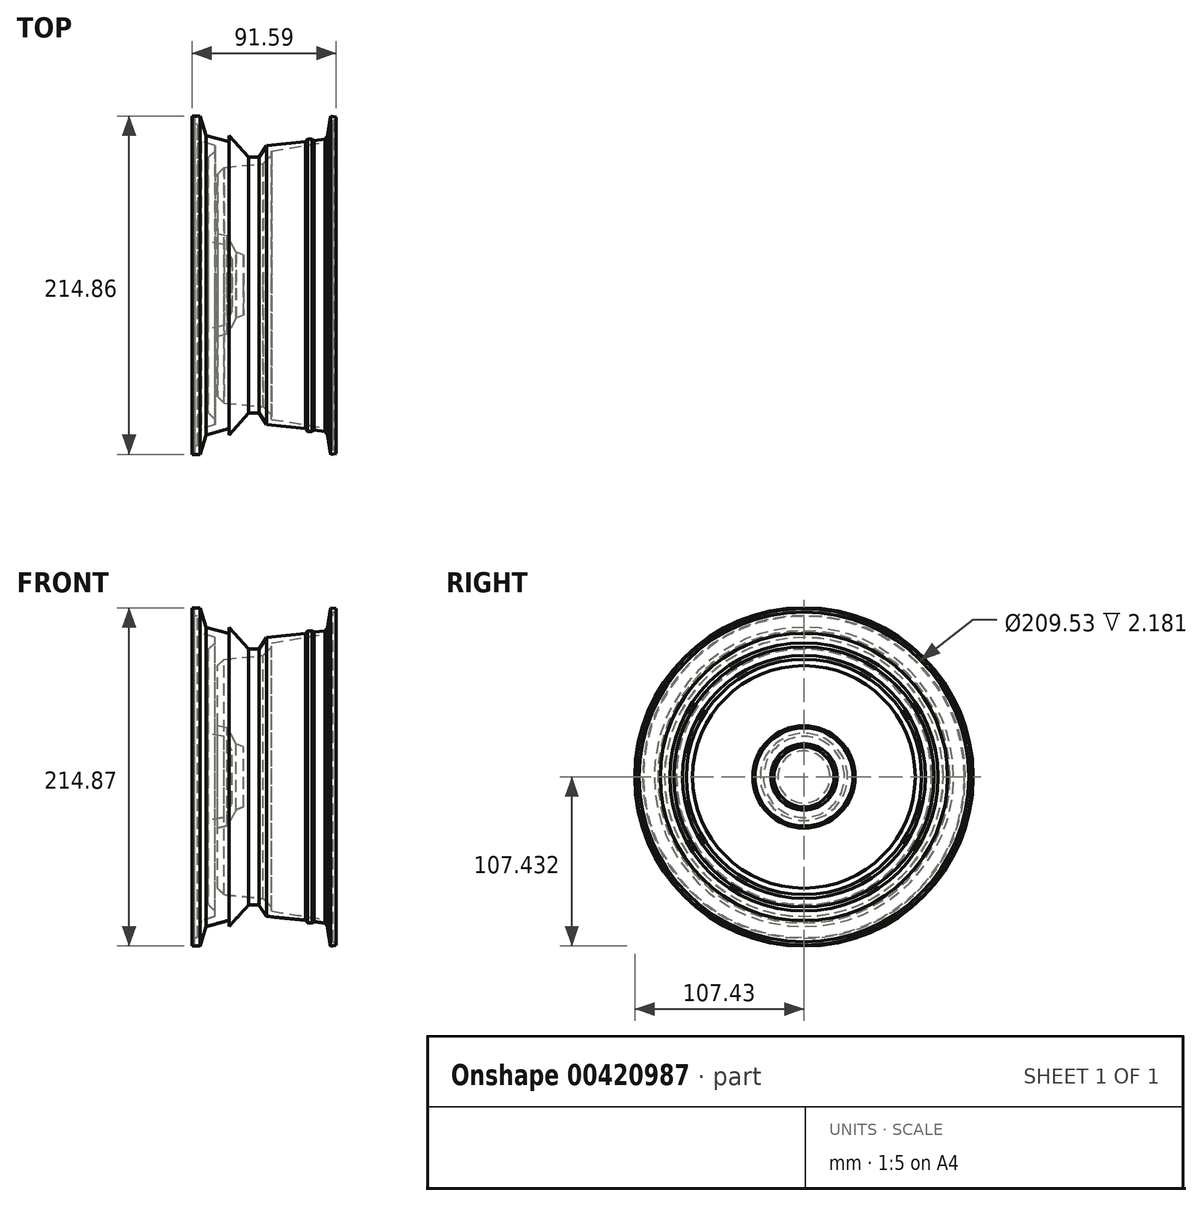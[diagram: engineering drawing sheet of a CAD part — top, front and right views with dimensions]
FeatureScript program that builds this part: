
annotation { "Feature Type Name" : "Feature", "Feature Type Description" : "" }
export const myFeature = defineFeature(function(context is Context, id is Id, definition is map)
    precondition{}
    {
        {
            var Q0;
            Q0=qCreatedBy(makeId("Front.planeOp"),FACE);
            var sketch = newSketch(context, id + "F0", { "sketchPlane" : qUnion([Q0])});
            skLineSegment(sketch, "E0", {"start": v(0, 70.08) * mm, "end": v(5.1, 70.08) * mm});
            skLineSegment(sketch, "E1", {"start": v(5.1, 70.08) * mm, "end": v(8.86, 57.73) * mm});
            skLineSegment(sketch, "E2", {"start": v(8.86, 57.73) * mm, "end": v(23.36, 53.7) * mm});
            skLineSegment(sketch, "E3", {"start": v(23.36, 53.7) * mm, "end": v(23.36, 57.73) * mm});
            skLineSegment(sketch, "E4", {"start": v(23.36, 57.73) * mm, "end": v(35.97, 43.93) * mm});
            skLineSegment(sketch, "E5", {"start": v(35.97, 43.93) * mm, "end": v(42.42, 43.93) * mm});
            skLineSegment(sketch, "E6", {"start": v(42.42, 43.93) * mm, "end": v(47.17, 51.15) * mm});
            skLineSegment(sketch, "E7", {"start": v(47.17, 51.15) * mm, "end": v(72.23, 53.7) * mm});
            skLineSegment(sketch, "E8", {"start": v(72.23, 53.7) * mm, "end": v(73.41, 55.5) * mm});
            skLineSegment(sketch, "E9", {"start": v(73.41, 55.5) * mm, "end": v(76.22, 55.5) * mm});
            skLineSegment(sketch, "E10", {"start": v(76.22, 55.5) * mm, "end": v(77.6, 54.58) * mm});
            skLineSegment(sketch, "E11", {"start": v(77.6, 54.58) * mm, "end": v(84.47, 55.5) * mm});
            skLineSegment(sketch, "E12", {"start": v(84.47, 55.5) * mm, "end": v(85.94, 57.73) * mm});
            skLineSegment(sketch, "E13", {"start": v(50.48, 47.84) * mm, "end": v(50.48, 45.28) * mm});
            skLineSegment(sketch, "E14", {"start": v(50.48, 45.28) * mm, "end": v(45.05, 39.85) * mm});
            skLineSegment(sketch, "E15", {"start": v(45.05, 39.85) * mm, "end": v(20.4, 37.38) * mm});
            skLineSegment(sketch, "E16", {"start": v(20.4, 37.38) * mm, "end": v(16.1, 33.31) * mm});
            skLineSegment(sketch, "E17", {"start": v(16.1, 33.31) * mm, "end": v(16.1, -4.84) * mm});
            skLineSegment(sketch, "E18", {"start": v(16.1, -4.84) * mm, "end": v(22.3, -6.17) * mm});
            skLineSegment(sketch, "E19", {"start": v(22.3, -6.17) * mm, "end": v(28.06, -16.4) * mm});
            skLineSegment(sketch, "E20", {"start": v(28.06, -16.4) * mm, "end": v(32.69, -18.3) * mm});
            skLineSegment(sketch, "E21", {"start": v(32.69, -18.3) * mm, "end": v(32.69, -37.36) * mm});
            skLineSegment(sketch, "E22", {"start": v(32.69, -37.36) * mm, "end": v(25.41, -37.36) * mm});
            skLineSegment(sketch, "E23", {"start": v(25.41, -37.36) * mm, "end": v(25.41, -20.88) * mm});
            skLineSegment(sketch, "E24", {"start": v(25.41, -20.88) * mm, "end": v(20.4, -11.62) * mm});
            skLineSegment(sketch, "E25", {"start": v(20.4, -11.62) * mm, "end": v(10.17, -9.66) * mm});
            skLineSegment(sketch, "E26", {"start": v(10.17, -9.66) * mm, "end": v(10.17, 43.69) * mm});
            skLineSegment(sketch, "E27", {"start": v(10.17, 43.69) * mm, "end": v(14.64, 47.84) * mm});
            skLineSegment(sketch, "E28", {"start": v(14.64, 47.84) * mm, "end": v(14.64, 51.23) * mm});
            skLineSegment(sketch, "E29", {"start": v(14.64, 51.23) * mm, "end": v(5.78, 54.05) * mm});
            skLineSegment(sketch, "E30", {"start": v(5.78, 54.05) * mm, "end": v(3.5, 64.65) * mm});
            skLineSegment(sketch, "E31", {"start": v(3.5, 64.65) * mm, "end": v(1.55, 65.2) * mm});
            skLineSegment(sketch, "E32", {"start": v(1.55, 65.2) * mm, "end": v(1.55, 69.02) * mm});
            skLineSegment(sketch, "E33", {"start": v(1.55, 69.02) * mm, "end": v(0, 68.68) * mm});
            skLineSegment(sketch, "E34", {"start": v(0, 68.68) * mm, "end": v(0, 70.08) * mm});
            skLineSegment(sketch, "E35", {"start": v(85.94, 57.73) * mm, "end": v(87.83, 70.08) * mm});
            skLineSegment(sketch, "E36", {"start": v(87.83, 70.08) * mm, "end": v(91.59, 69.5) * mm});
            skLineSegment(sketch, "E37", {"start": v(91.59, 69.5) * mm, "end": v(91.59, 67.4) * mm});
            skLineSegment(sketch, "E38", {"start": v(91.59, 67.4) * mm, "end": v(89.4, 67.4) * mm});
            skLineSegment(sketch, "E39", {"start": v(89.4, 67.4) * mm, "end": v(87.83, 53.9) * mm});
            skLineSegment(sketch, "E40", {"start": v(87.83, 53.9) * mm, "end": v(50.48, 47.84) * mm});
            skSolve(sketch);
        }
        {
            var Q0;
            Q0=makeQuery(id+"F0.imprint","IMPRINT",FACE,{"disambiguationData":[TD([[makeQuery(id+"F0.imprint","IMPRINT",EDGE,{"derivedFrom":sQuery(id+"F0.wireOp",EDGE,"E0")}),-1.0]])]});
            var Q1;
            Q1=sQuery(id+"F0.wireOp",EDGE,"E22");
            revolve(context, id + "F1", {"entities" : qUnion([Q0]), "axis" : qUnion([Q1]), "revolveType" : RevolveType.FULL});
        }
    });
